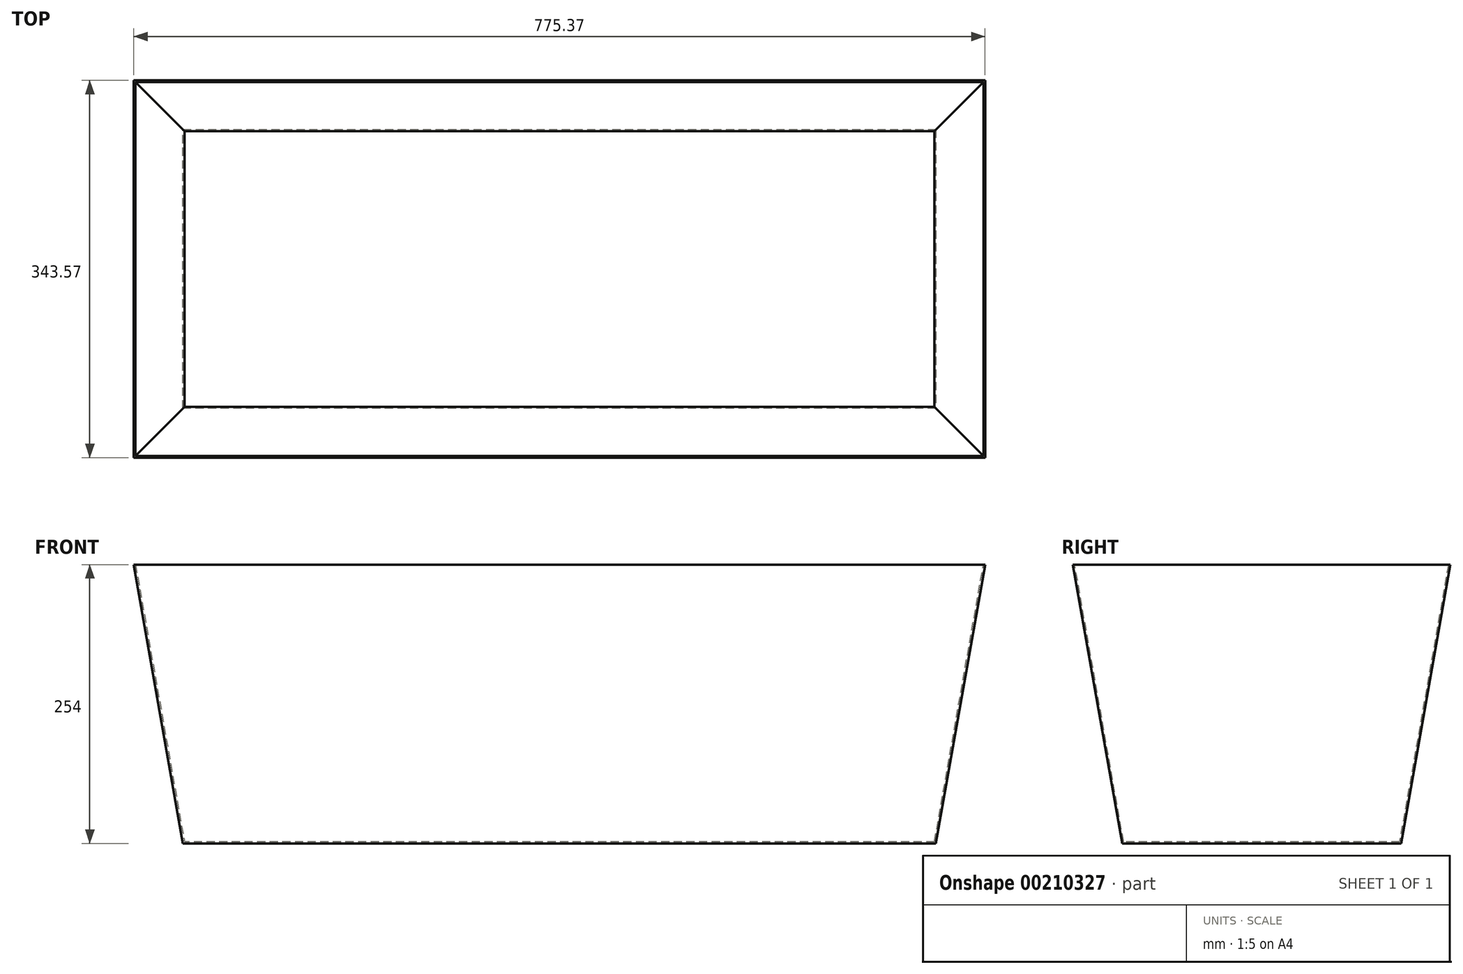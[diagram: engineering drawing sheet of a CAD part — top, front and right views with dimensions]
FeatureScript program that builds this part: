
annotation { "Feature Type Name" : "Feature", "Feature Type Description" : "" }
export const myFeature = defineFeature(function(context is Context, id is Id, definition is map)
    precondition{}
    {
        {
            var Q0;
            Q0=qCreatedBy(makeId("Top.planeOp"),FACE);
            var sketch = newSketch(context, id + "F0", { "sketchPlane" : qUnion([Q0])});
            skLineSegment(sketch, "E0.bottom", {"start": v(-337.06, 76.3) * mm, "end": v(348.74, 76.3) * mm});
            skLineSegment(sketch, "E0.top", {"start": v(-337.06, -177.7) * mm, "end": v(348.74, -177.7) * mm});
            skLineSegment(sketch, "E0.left", {"start": v(-337.06, 76.3) * mm, "end": v(-337.06, -177.7) * mm});
            skLineSegment(sketch, "E0.right", {"start": v(348.74, 76.3) * mm, "end": v(348.74, -177.7) * mm});
            skSolve(sketch);
        }
        {
            var Q0;
            Q0 = qSketchRegion(id + "F0", true);
            extrude(context, id + "F1", {"entities" : qUnion([Q0]), "depth" : 254 * mm, "hasDraft" : true, "draftAngle" : 10 * degree});
        }
        {
            var Q0;
            Q0=makeQuery(id+"F1.opExtrude","CAP_FACE",FACE,{"disambiguationData":[OSD([sQuery(id+"F0.wireOp",EDGE,"E0.bottom"),sQuery(id+"F0.wireOp",EDGE,"E0.top"),sQuery(id+"F0.wireOp",EDGE,"E0.left"),sQuery(id+"F0.wireOp",EDGE,"E0.right")])],"isStart":false});
            var sketch = newSketch(context, id + "F2", { "sketchPlane" : qUnion([Q0])});
            skLineSegment(sketch, "E1.0", {"start": v(-380.26, 119.5) * mm, "end": v(391.94, 119.5) * mm});
            skLineSegment(sketch, "E1.1", {"start": v(-380.26, 119.5) * mm, "end": v(-380.26, -220.9) * mm});
            skLineSegment(sketch, "E1.2", {"start": v(-380.26, -220.9) * mm, "end": v(391.94, -220.9) * mm});
            skLineSegment(sketch, "E2.0", {"start": v(391.94, 119.5) * mm, "end": v(391.94, -220.9) * mm});
            skSolve(sketch);
        }
        {
            var Q0;
            Q0 = qSketchRegion(id + "F2", true);
            extrude(context, id + "F3", {"entities" : qUnion([Q0]), "operationType" : NewBodyOperationType.REMOVE, "oppositeDirection" : true, "depth" : 252.4 * mm, "hasDraft" : true, "draftAngle" : 10 * degree, "draftPullDirection" : true});
        }
    });
